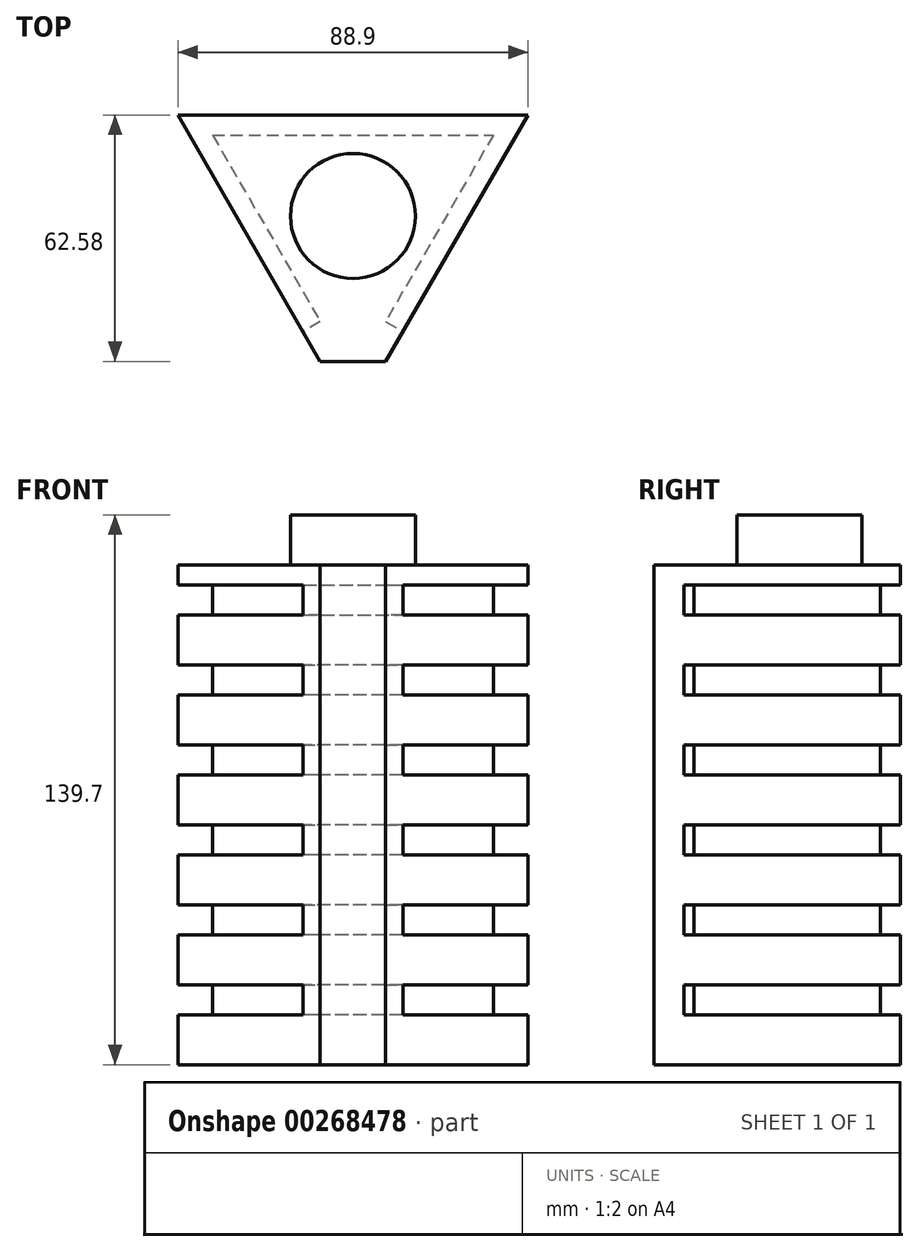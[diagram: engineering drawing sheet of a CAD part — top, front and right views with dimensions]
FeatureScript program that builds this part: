
annotation { "Feature Type Name" : "Feature", "Feature Type Description" : "" }
export const myFeature = defineFeature(function(context is Context, id is Id, definition is map)
    precondition{}
    {
        {
            var Q0;
            Q0=qCreatedBy(makeId("Top.planeOp"),FACE);
            var sketch = newSketch(context, id + "F0", { "sketchPlane" : qUnion([Q0])});
            skCircle(sketch, "E0.cCircle", {"center": v(0, 0) * mm, "radius": 25.66 * mm, "construction": true});
            skLineSegment(sketch, "E0.0", {"start": v(-44.45, 25.66) * mm, "end": v(44.45, 25.66) * mm});
            skLineSegment(sketch, "E0.1", {"start": v(44.45, 25.66) * mm, "end": v(0, -51.33) * mm});
            skLineSegment(sketch, "E0.2", {"start": v(0, -51.33) * mm, "end": v(-44.45, 25.66) * mm});
            skPoint(sketch, "E0.0.midPoint", {"position": v(0, 25.66) * mm});
            skSolve(sketch);
        }
        {
            var Q0;
            Q0=qSketchRegion(id+"F0",true);
            extrude(context, id + "F1", {"entities" : qUnion([Q0]), "depth" : 127 * mm});
        }
        {
            var Q0;
            Q0=qCreatedBy(makeId("Top.planeOp"),FACE);
            var sketch = newSketch(context, id + "F2", { "sketchPlane" : qUnion([Q0])});
            skLineSegment(sketch, "E1.bottom", {"start": v(-45.03, 26.58) * mm, "end": v(44.53, 26.58) * mm});
            skLineSegment(sketch, "E1.top", {"start": v(-45.03, -36.92) * mm, "end": v(44.53, -36.92) * mm});
            skLineSegment(sketch, "E1.left", {"start": v(-45.03, 26.58) * mm, "end": v(-45.03, -36.92) * mm});
            skLineSegment(sketch, "E1.right", {"start": v(44.53, 26.58) * mm, "end": v(44.53, -36.92) * mm});
            skSolve(sketch);
        }
        {
            var Q0;
            Q0=qSketchRegion(id+"F2",true);
            extrude(context, id + "F3", {"entities" : qUnion([Q0]), "operationType" : NewBodyOperationType.INTERSECT, "depth" : 215.9 * mm});
        }
        {
            var Q0;
            Q0=qCreatedBy(makeId("Top.planeOp"),FACE);
            var sketch = newSketch(context, id + "F4", { "sketchPlane" : qUnion([Q0])});
            skCircle(sketch, "E2", {"center": v(0, 0) * mm, "radius": 15.88 * mm});
            skSolve(sketch);
        }
        {
            var Q0;
            Q0=qSketchRegion(id+"F4",true);
            extrude(context, id + "F5", {"entities" : qUnion([Q0]), "operationType" : NewBodyOperationType.ADD, "depth" : 139.7 * mm});
        }
        {
            var Q0;
            Q0=makeQuery(id+"F1.opExtrude","SWEPT_FACE",FACE,{"disambiguationData":[OSD([sQuery(id+"F0.wireOp",EDGE,"E0.0")])]});
            var sketch = newSketch(context, id + "F6", { "sketchPlane" : qUnion([Q0])});
            skLineSegment(sketch, "E3.bottom", {"start": v(-44.45, 0) * mm, "end": v(44.45, 0) * mm, "construction": true});
            skLineSegment(sketch, "E3.top", {"start": v(-44.45, 12.7) * mm, "end": v(44.45, 12.7) * mm, "construction": true});
            skLineSegment(sketch, "E3.left", {"start": v(-44.45, 0) * mm, "end": v(-44.45, 12.7) * mm, "construction": true});
            skLineSegment(sketch, "E3.right", {"start": v(44.45, 0) * mm, "end": v(44.45, 12.7) * mm, "construction": true});
            skLineSegment(sketch, "E4.bottom", {"start": v(-44.45, 12.7) * mm, "end": v(44.45, 12.7) * mm});
            skLineSegment(sketch, "E4.top", {"start": v(-44.45, 20.32) * mm, "end": v(44.45, 20.32) * mm});
            skLineSegment(sketch, "E4.left", {"start": v(-44.45, 12.7) * mm, "end": v(-44.45, 20.32) * mm});
            skLineSegment(sketch, "E4.right", {"start": v(44.45, 12.7) * mm, "end": v(44.45, 20.32) * mm});
            skLineSegment(sketch, "E5.bottom", {"start": v(-44.45, 20.32) * mm, "end": v(44.45, 20.32) * mm, "construction": true});
            skLineSegment(sketch, "E5.top", {"start": v(-44.45, 33.02) * mm, "end": v(44.45, 33.02) * mm, "construction": true});
            skLineSegment(sketch, "E5.left", {"start": v(-44.45, 20.32) * mm, "end": v(-44.45, 33.02) * mm, "construction": true});
            skLineSegment(sketch, "E5.right", {"start": v(44.45, 20.32) * mm, "end": v(44.45, 33.02) * mm, "construction": true});
            skLineSegment(sketch, "E6.bottom", {"start": v(-44.45, 33.02) * mm, "end": v(44.45, 33.02) * mm});
            skLineSegment(sketch, "E6.top", {"start": v(-44.45, 40.64) * mm, "end": v(44.45, 40.64) * mm});
            skLineSegment(sketch, "E6.left", {"start": v(-44.45, 33.02) * mm, "end": v(-44.45, 40.64) * mm});
            skLineSegment(sketch, "E6.right", {"start": v(44.45, 33.02) * mm, "end": v(44.45, 40.64) * mm});
            skLineSegment(sketch, "E7.bottom", {"start": v(-44.45, 40.64) * mm, "end": v(44.45, 40.64) * mm, "construction": true});
            skLineSegment(sketch, "E7.top", {"start": v(-44.45, 53.34) * mm, "end": v(44.45, 53.34) * mm, "construction": true});
            skLineSegment(sketch, "E7.left", {"start": v(-44.45, 40.64) * mm, "end": v(-44.45, 53.34) * mm, "construction": true});
            skLineSegment(sketch, "E7.right", {"start": v(44.45, 40.64) * mm, "end": v(44.45, 53.34) * mm, "construction": true});
            skLineSegment(sketch, "E8.bottom", {"start": v(-44.45, 53.34) * mm, "end": v(44.45, 53.34) * mm});
            skLineSegment(sketch, "E8.top", {"start": v(-44.45, 60.96) * mm, "end": v(44.45, 60.96) * mm});
            skLineSegment(sketch, "E8.left", {"start": v(-44.45, 53.34) * mm, "end": v(-44.45, 60.96) * mm});
            skLineSegment(sketch, "E8.right", {"start": v(44.45, 53.34) * mm, "end": v(44.45, 60.96) * mm});
            skLineSegment(sketch, "E9.bottom", {"start": v(-44.45, 60.96) * mm, "end": v(44.45, 60.96) * mm, "construction": true});
            skLineSegment(sketch, "E9.top", {"start": v(-44.45, 73.66) * mm, "end": v(44.45, 73.66) * mm, "construction": true});
            skLineSegment(sketch, "E9.left", {"start": v(-44.45, 60.96) * mm, "end": v(-44.45, 73.66) * mm, "construction": true});
            skLineSegment(sketch, "E9.right", {"start": v(44.45, 60.96) * mm, "end": v(44.45, 73.66) * mm, "construction": true});
            skLineSegment(sketch, "E10.bottom", {"start": v(-44.45, 73.66) * mm, "end": v(44.45, 73.66) * mm});
            skLineSegment(sketch, "E10.top", {"start": v(-44.45, 81.28) * mm, "end": v(44.45, 81.28) * mm});
            skLineSegment(sketch, "E10.left", {"start": v(-44.45, 73.66) * mm, "end": v(-44.45, 81.28) * mm});
            skLineSegment(sketch, "E10.right", {"start": v(44.45, 73.66) * mm, "end": v(44.45, 81.28) * mm});
            skLineSegment(sketch, "E11.bottom", {"start": v(-44.45, 81.28) * mm, "end": v(44.45, 81.28) * mm, "construction": true});
            skLineSegment(sketch, "E11.top", {"start": v(-44.45, 93.98) * mm, "end": v(44.45, 93.98) * mm, "construction": true});
            skLineSegment(sketch, "E11.left", {"start": v(-44.45, 81.28) * mm, "end": v(-44.45, 93.98) * mm, "construction": true});
            skLineSegment(sketch, "E11.right", {"start": v(44.45, 81.28) * mm, "end": v(44.45, 93.98) * mm, "construction": true});
            skLineSegment(sketch, "E12.bottom", {"start": v(-44.45, 93.98) * mm, "end": v(44.45, 93.98) * mm});
            skLineSegment(sketch, "E12.top", {"start": v(-44.45, 101.6) * mm, "end": v(44.45, 101.6) * mm});
            skLineSegment(sketch, "E12.left", {"start": v(-44.45, 93.98) * mm, "end": v(-44.45, 101.6) * mm});
            skLineSegment(sketch, "E12.right", {"start": v(44.45, 93.98) * mm, "end": v(44.45, 101.6) * mm});
            skLineSegment(sketch, "E13.bottom", {"start": v(44.45, 101.6) * mm, "end": v(-44.45, 101.6) * mm, "construction": true});
            skLineSegment(sketch, "E13.top", {"start": v(44.45, 114.3) * mm, "end": v(-44.45, 114.3) * mm, "construction": true});
            skLineSegment(sketch, "E13.left", {"start": v(44.45, 101.6) * mm, "end": v(44.45, 114.3) * mm, "construction": true});
            skLineSegment(sketch, "E13.right", {"start": v(-44.45, 101.6) * mm, "end": v(-44.45, 114.3) * mm, "construction": true});
            skLineSegment(sketch, "E14.bottom", {"start": v(44.45, 114.3) * mm, "end": v(-44.45, 114.3) * mm});
            skLineSegment(sketch, "E14.top", {"start": v(44.45, 121.92) * mm, "end": v(-44.45, 121.92) * mm});
            skLineSegment(sketch, "E14.left", {"start": v(44.45, 114.3) * mm, "end": v(44.45, 121.92) * mm});
            skLineSegment(sketch, "E14.right", {"start": v(-44.45, 114.3) * mm, "end": v(-44.45, 121.92) * mm});
            skSolve(sketch);
        }
        {
            var Q0;
            Q0 = qSketchRegion(id + "F6", true);
            extrude(context, id + "F7", {"entities" : qUnion([Q0]), "operationType" : NewBodyOperationType.REMOVE, "oppositeDirection" : true, "depth" : 5.08 * mm});
        }
        {
            var Q0;
            Q0=makeQuery(id+"F1.opExtrude","SWEPT_FACE",FACE,{"disambiguationData":[OSD([sQuery(id+"F0.wireOp",EDGE,"E0.1")])]});
            var sketch = newSketch(context, id + "F8", { "sketchPlane" : qUnion([Q0])});
            skLineSegment(sketch, "E15.bottom", {"start": v(44.45, 20.32) * mm, "end": v(-19.05, 20.32) * mm});
            skLineSegment(sketch, "E15.top", {"start": v(44.45, 12.7) * mm, "end": v(-19.05, 12.7) * mm});
            skLineSegment(sketch, "E15.left", {"start": v(44.45, 20.32) * mm, "end": v(44.45, 12.7) * mm});
            skLineSegment(sketch, "E15.right", {"start": v(-19.05, 20.32) * mm, "end": v(-19.05, 12.7) * mm});
            skPoint(sketch, "E16.oppositeSnap0", {"position": v(41.52, 40.64) * mm});
            skLineSegment(sketch, "E16.bottom", {"start": v(44.45, 33.02) * mm, "end": v(-19.05, 33.02) * mm});
            skLineSegment(sketch, "E16.top", {"start": v(44.45, 40.64) * mm, "end": v(-19.05, 40.64) * mm});
            skLineSegment(sketch, "E16.left", {"start": v(44.45, 33.02) * mm, "end": v(44.45, 40.64) * mm});
            skLineSegment(sketch, "E16.right", {"start": v(-19.05, 33.02) * mm, "end": v(-19.05, 40.64) * mm});
            skLineSegment(sketch, "E17.bottom", {"start": v(44.45, 53.34) * mm, "end": v(-19.05, 53.34) * mm});
            skLineSegment(sketch, "E17.top", {"start": v(44.45, 60.96) * mm, "end": v(-19.05, 60.96) * mm});
            skLineSegment(sketch, "E17.left", {"start": v(44.45, 53.34) * mm, "end": v(44.45, 60.96) * mm});
            skLineSegment(sketch, "E17.right", {"start": v(-19.05, 53.34) * mm, "end": v(-19.05, 60.96) * mm});
            skLineSegment(sketch, "E18.bottom", {"start": v(44.45, 73.66) * mm, "end": v(-19.05, 73.66) * mm});
            skLineSegment(sketch, "E18.top", {"start": v(44.45, 81.28) * mm, "end": v(-19.05, 81.28) * mm});
            skLineSegment(sketch, "E18.left", {"start": v(44.45, 73.66) * mm, "end": v(44.45, 81.28) * mm});
            skLineSegment(sketch, "E18.right", {"start": v(-19.05, 73.66) * mm, "end": v(-19.05, 81.28) * mm});
            skLineSegment(sketch, "E19.bottom", {"start": v(44.45, 93.98) * mm, "end": v(-19.05, 93.98) * mm});
            skLineSegment(sketch, "E19.top", {"start": v(44.45, 101.6) * mm, "end": v(-19.05, 101.6) * mm});
            skLineSegment(sketch, "E19.left", {"start": v(44.45, 93.98) * mm, "end": v(44.45, 101.6) * mm});
            skLineSegment(sketch, "E19.right", {"start": v(-19.05, 93.98) * mm, "end": v(-19.05, 101.6) * mm});
            skLineSegment(sketch, "E20.bottom", {"start": v(44.45, 114.3) * mm, "end": v(-19.05, 114.3) * mm});
            skLineSegment(sketch, "E20.top", {"start": v(44.45, 121.92) * mm, "end": v(-19.05, 121.92) * mm});
            skLineSegment(sketch, "E20.left", {"start": v(44.45, 114.3) * mm, "end": v(44.45, 121.92) * mm});
            skLineSegment(sketch, "E20.right", {"start": v(-19.05, 114.3) * mm, "end": v(-19.05, 121.92) * mm});
            skSolve(sketch);
        }
        {
            var Q0;
            Q0 = qSketchRegion(id + "F8", true);
            extrude(context, id + "F9", {"entities" : qUnion([Q0]), "operationType" : NewBodyOperationType.REMOVE, "oppositeDirection" : true, "depth" : 5.08 * mm});
        }
        {
            var Q0;
            Q0=makeQuery(id+"F1.opExtrude","SWEPT_FACE",FACE,{"disambiguationData":[OSD([sQuery(id+"F0.wireOp",EDGE,"E0.2")])]});
            var sketch = newSketch(context, id + "F10", { "sketchPlane" : qUnion([Q0])});
            skLineSegment(sketch, "E21.bottom", {"start": v(-44.45, 12.7) * mm, "end": v(19.05, 12.7) * mm});
            skLineSegment(sketch, "E21.top", {"start": v(-44.45, 20.32) * mm, "end": v(19.05, 20.32) * mm});
            skLineSegment(sketch, "E21.left", {"start": v(-44.45, 12.7) * mm, "end": v(-44.45, 20.32) * mm});
            skLineSegment(sketch, "E21.right", {"start": v(19.05, 12.7) * mm, "end": v(19.05, 20.32) * mm});
            skLineSegment(sketch, "E22.bottom", {"start": v(-44.45, 33.02) * mm, "end": v(19.05, 33.02) * mm});
            skLineSegment(sketch, "E22.top", {"start": v(-44.45, 40.64) * mm, "end": v(19.05, 40.64) * mm});
            skLineSegment(sketch, "E22.left", {"start": v(-44.45, 33.02) * mm, "end": v(-44.45, 40.64) * mm});
            skLineSegment(sketch, "E22.right", {"start": v(19.05, 33.02) * mm, "end": v(19.05, 40.64) * mm});
            skLineSegment(sketch, "E23.bottom", {"start": v(-44.45, 53.34) * mm, "end": v(19.05, 53.34) * mm});
            skLineSegment(sketch, "E23.top", {"start": v(-44.45, 60.96) * mm, "end": v(19.05, 60.96) * mm});
            skLineSegment(sketch, "E23.left", {"start": v(-44.45, 53.34) * mm, "end": v(-44.45, 60.96) * mm});
            skLineSegment(sketch, "E23.right", {"start": v(19.05, 53.34) * mm, "end": v(19.05, 60.96) * mm});
            skLineSegment(sketch, "E24.bottom", {"start": v(-44.45, 73.66) * mm, "end": v(19.05, 73.66) * mm});
            skLineSegment(sketch, "E24.top", {"start": v(-44.45, 81.28) * mm, "end": v(19.05, 81.28) * mm});
            skLineSegment(sketch, "E24.left", {"start": v(-44.45, 73.66) * mm, "end": v(-44.45, 81.28) * mm});
            skLineSegment(sketch, "E24.right", {"start": v(19.05, 73.66) * mm, "end": v(19.05, 81.28) * mm});
            skLineSegment(sketch, "E25.bottom", {"start": v(-44.45, 93.98) * mm, "end": v(19.05, 93.98) * mm});
            skLineSegment(sketch, "E25.top", {"start": v(-44.45, 101.6) * mm, "end": v(19.05, 101.6) * mm});
            skLineSegment(sketch, "E25.left", {"start": v(-44.45, 93.98) * mm, "end": v(-44.45, 101.6) * mm});
            skLineSegment(sketch, "E25.right", {"start": v(19.05, 93.98) * mm, "end": v(19.05, 101.6) * mm});
            skLineSegment(sketch, "E26.bottom", {"start": v(-44.45, 114.3) * mm, "end": v(19.05, 114.3) * mm});
            skLineSegment(sketch, "E26.top", {"start": v(-44.45, 121.92) * mm, "end": v(19.05, 121.92) * mm});
            skLineSegment(sketch, "E26.left", {"start": v(-44.45, 114.3) * mm, "end": v(-44.45, 121.92) * mm});
            skLineSegment(sketch, "E26.right", {"start": v(19.05, 114.3) * mm, "end": v(19.05, 121.92) * mm});
            skSolve(sketch);
        }
        {
            var Q0;
            Q0 = qSketchRegion(id + "F10", true);
            extrude(context, id + "F11", {"entities" : qUnion([Q0]), "operationType" : NewBodyOperationType.REMOVE, "oppositeDirection" : true, "depth" : 5.08 * mm});
        }
    });
